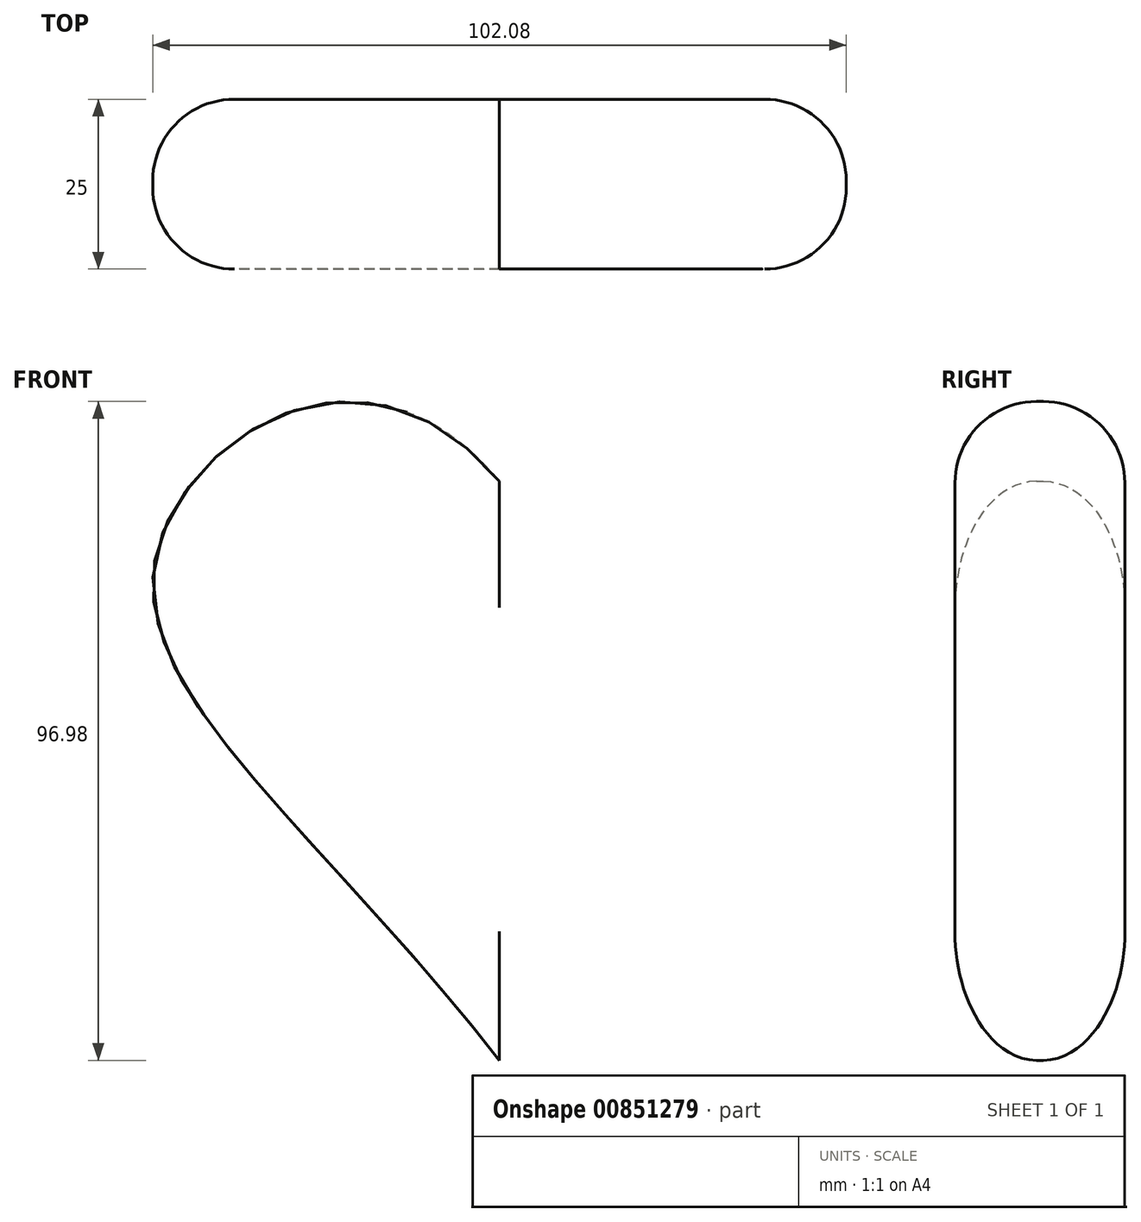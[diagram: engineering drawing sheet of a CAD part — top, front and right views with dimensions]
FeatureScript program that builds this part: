
annotation { "Feature Type Name" : "Feature", "Feature Type Description" : "" }
export const myFeature = defineFeature(function(context is Context, id is Id, definition is map)
    precondition{}
    {
        {
            var Q0;
            Q0=qCreatedBy(makeId("Front.planeOp"),FACE);
            var sketch = newSketch(context, id + "F0", { "sketchPlane" : qUnion([Q0])});
            skFitSpline(sketch, "E0", {"points": [v(0, 0) * mm, v(-50, 76.47) * mm, v(0, 85.25) * mm], "startDerivative": vector(-147.07, 188.19) * mm, "endDerivative": vector(139.36, -165.38) * mm});
            skFitSpline(sketch, "E1.MirrorCS", {"points": [v(0, 0) * mm, v(50, 76.47) * mm, v(0, 85.25) * mm], "startDerivative": vector(147.07, 188.19) * mm, "endDerivative": vector(-139.36, -165.38) * mm});
            skSolve(sketch);
        }
        {
            var Q0;
            Q0=qSketchRegion(id+"F0",true);
            extrude(context, id + "F1", {"entities" : qUnion([Q0]), "offsetDistance" : 25 * mm, "depth" : 25 * mm});
        }
        {
            var Q0;
            Q0=makeQuery(id+"F1.opExtrude","CAP_EDGE",EDGE,{"disambiguationData":[OSD([sQuery(id+"F0.wireOp",EDGE,"E0")])],"isStart":false});
            var Q1;
            Q1=makeQuery(id+"F1.opExtrude","CAP_EDGE",EDGE,{"disambiguationData":[OSD([sQuery(id+"F0.wireOp",EDGE,"E1.MirrorCS")])],"isStart":false});
            var Q2;
            Q2=makeQuery(id+"F1.opExtrude","CAP_EDGE",EDGE,{"disambiguationData":[OSD([sQuery(id+"F0.wireOp",EDGE,"E1.MirrorCS")])],"isStart":true});
            var Q3;
            Q3=makeQuery(id+"F1.opExtrude","CAP_EDGE",EDGE,{"disambiguationData":[OSD([sQuery(id+"F0.wireOp",EDGE,"E0")])],"isStart":true});
            fillet(context, id + "F2", {"entities" : qUnion([Q0, Q1, Q2, Q3]), "radius" : 12 * mm, "tangentPropagation" : true, "allowEdgeOverflow" : false});
        }
    });
